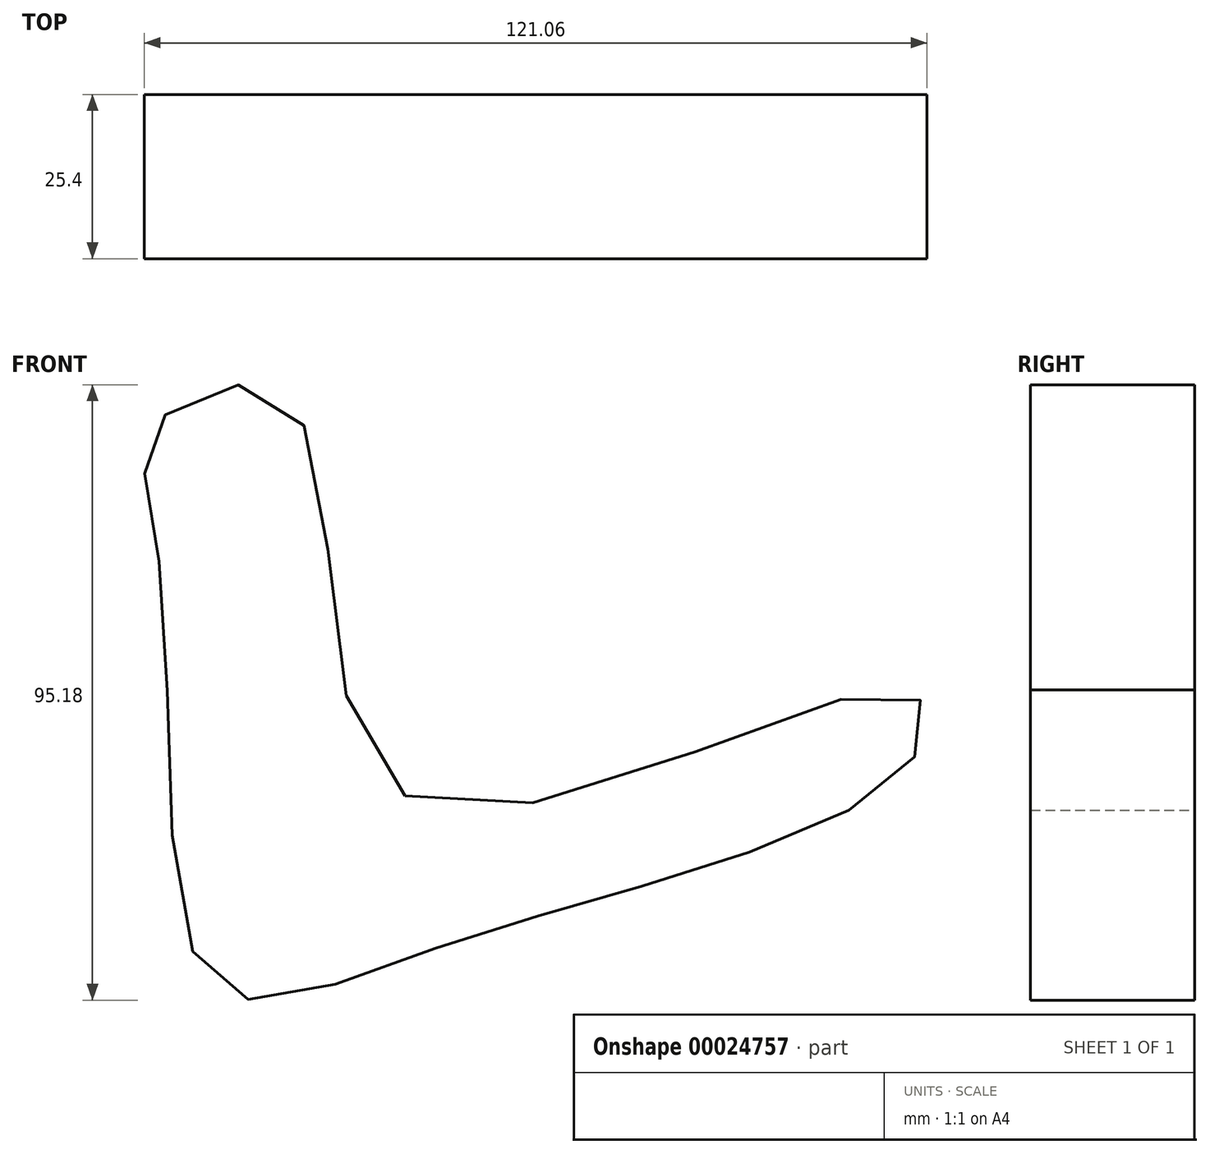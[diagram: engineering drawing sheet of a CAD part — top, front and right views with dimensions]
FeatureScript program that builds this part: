
annotation { "Feature Type Name" : "Feature", "Feature Type Description" : "" }
export const myFeature = defineFeature(function(context is Context, id is Id, definition is map)
    precondition{}
    {
        {
            var Q0;
            Q0=qCreatedBy(makeId("Front.planeOp"),FACE);
            var sketch = newSketch(context, id + "F0", { "sketchPlane" : qUnion([Q0])});
            skFitSpline(sketch, "E0", {"points": [v(-65.89, 35.1) * mm, v(11.12, 51.34) * mm, v(13.26, 41.7) * mm, v(-20.96, 23.68) * mm, v(-66.31, 9.74) * mm, v(-95.84, 6.35) * mm, v(-103.54, 68.3) * mm, v(-103.96, 93) * mm, v(-83.43, 95.5) * mm, v(-65.89, 35.1) * mm]});
            skSolve(sketch);
        }
        {
            var Q0;
            Q0 = qSketchRegion(id + "F0", true);
            extrude(context, id + "F1", {"entities" : qUnion([Q0]), "depth" : 25.4 * mm});
        }
    });
